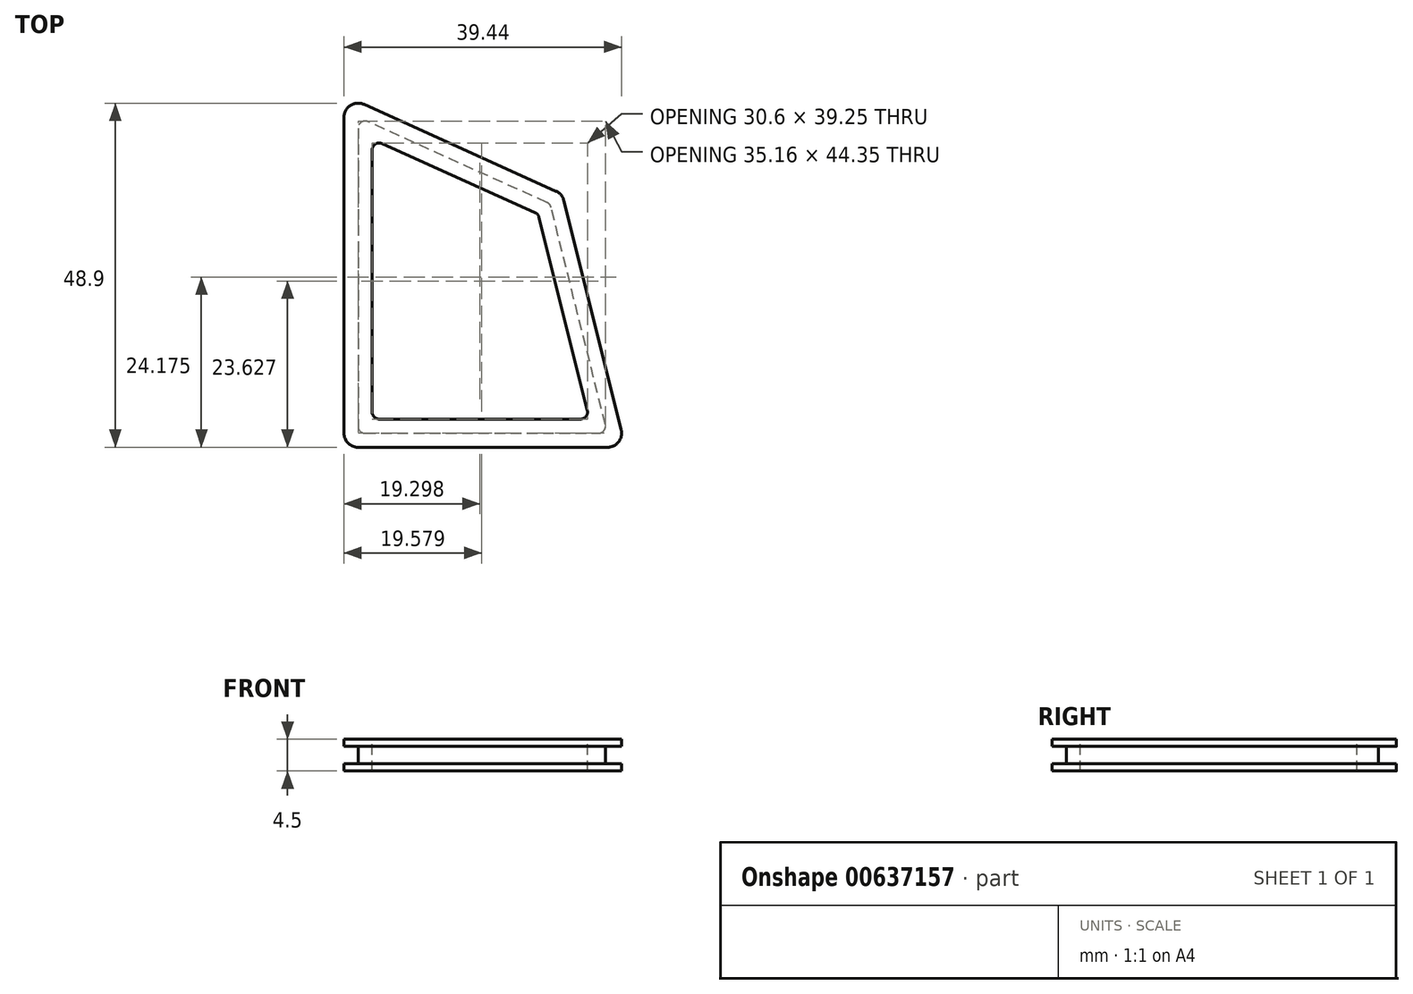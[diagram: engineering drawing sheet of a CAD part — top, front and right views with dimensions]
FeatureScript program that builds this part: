
annotation { "Feature Type Name" : "Feature", "Feature Type Description" : "" }
export const myFeature = defineFeature(function(context is Context, id is Id, definition is map)
    precondition{}
    {
        {
            var Q0;
            Q0=qCreatedBy(makeId("Top.planeOp"),FACE);
            var sketch = newSketch(context, id + "F0", { "sketchPlane" : qUnion([Q0])});
            skLineSegment(sketch, "E0.bottom", {"start": v(17.44, -25) * mm, "end": v(-18, -25) * mm});
            skLineSegment(sketch, "E0.top", {"start": v(10.12, 11.4) * mm, "end": v(-17.18, 23.73) * mm});
            skLineSegment(sketch, "E0.left", {"start": v(19.38, -22.51) * mm, "end": v(11.23, 10.06) * mm});
            skLineSegment(sketch, "E0.right", {"start": v(-20, -23) * mm, "end": v(-20, 21.9) * mm});
            skPoint(sketch, "E0.middle", {"position": v(0, 0) * mm});
            skPoint(sketch, "E1.visualSharp", {"position": v(-20, 25) * mm});
            skArc(sketch, "E1.filletArc", {"start": v(-17.18, 23.73) * mm, "mid": v(-19.08, 23.58) * mm, "end": v(-20, 21.9) * mm});
            skPoint(sketch, "E2.visualSharp", {"position": v(-20, -25) * mm});
            skArc(sketch, "E2.filletArc", {"start": v(-20, -23) * mm, "mid": v(-19.41, -24.41) * mm, "end": v(-18, -25) * mm});
            skPoint(sketch, "E3.visualSharp", {"position": v(20, -25) * mm});
            skArc(sketch, "E3.filletArc", {"start": v(17.44, -25) * mm, "mid": v(19.01, -24.23) * mm, "end": v(19.38, -22.51) * mm});
            skPoint(sketch, "E4.visualSharp", {"position": v(11, 11) * mm});
            skArc(sketch, "E4.filletArc", {"start": v(11.23, 10.06) * mm, "mid": v(10.83, 10.86) * mm, "end": v(10.12, 11.4) * mm});
            skSolve(sketch);
        }
        {
            var Q0;
            Q0=qCreatedBy(makeId("Top.planeOp"),FACE);
            var sketch = newSketch(context, id + "F1", { "sketchPlane" : qUnion([Q0])});
            skLineSegment(sketch, "E5.0.1", {"start": v(8.85, 9.77) * mm, "end": v(-16.59, 21.26) * mm});
            skLineSegment(sketch, "E5.0.3", {"start": v(-18, 20.35) * mm, "end": v(-18, -22) * mm});
            skLineSegment(sketch, "E5.0.5", {"start": v(-17, -23) * mm, "end": v(16.16, -23) * mm});
            skLineSegment(sketch, "E5.0.7", {"start": v(17.13, -21.76) * mm, "end": v(9.41, 9.1) * mm});
            skPoint(sketch, "E6.visualSharp", {"position": v(-18, 21.9) * mm});
            skArc(sketch, "E6.filletArc", {"start": v(-16.59, 21.26) * mm, "mid": v(-17.54, 21.2) * mm, "end": v(-18, 20.35) * mm});
            skPoint(sketch, "E7.visualSharp", {"position": v(9.3, 9.58) * mm});
            skArc(sketch, "E7.filletArc", {"start": v(9.41, 9.1) * mm, "mid": v(9.2, 9.5) * mm, "end": v(8.85, 9.77) * mm});
            skPoint(sketch, "E8.visualSharp", {"position": v(-18, -23) * mm});
            skArc(sketch, "E8.filletArc", {"start": v(-18, -22) * mm, "mid": v(-17.7, -22.7) * mm, "end": v(-17, -23) * mm});
            skPoint(sketch, "E9.visualSharp", {"position": v(17.44, -23) * mm});
            skArc(sketch, "E9.filletArc", {"start": v(16.16, -23) * mm, "mid": v(16.95, -22.62) * mm, "end": v(17.13, -21.76) * mm});
            skSolve(sketch);
        }
        {
            var Q0;
            Q0=makeQuery(id+"F1.imprint","IMPRINT",FACE,{"disambiguationData":[TD([[makeQuery(id+"F1.imprint","IMPRINT",EDGE,{"derivedFrom":sQuery(id+"F1.wireOp",EDGE,"E5.0.1")}),1.0]])]});
            extrude(context, id + "F2", {"entities" : qUnion([Q0]), "depth" : 2.5 * mm, "offsetDistance" : 25 * mm});
        }
        {
            var Q0;
            Q0=makeQuery(id+"F0.imprint","IMPRINT",FACE,{"disambiguationData":[TD([[makeQuery(id+"F0.imprint","IMPRINT",EDGE,{"derivedFrom":sQuery(id+"F0.wireOp",EDGE,"E0.bottom")}),-1.0]])]});
            extrude(context, id + "F3", {"entities" : qUnion([Q0]), "operationType" : NewBodyOperationType.ADD, "oppositeDirection" : true, "depth" : 1 * mm, "offsetDistance" : 25 * mm});
        }
        {
            var Q0;
            Q0=makeQuery(id+"F2.opExtrude","CAP_FACE",FACE,{"disambiguationData":[OSD([sQuery(id+"F1.wireOp",EDGE,"E5.0.1"),sQuery(id+"F1.wireOp",EDGE,"E5.0.3"),sQuery(id+"F1.wireOp",EDGE,"E5.0.5"),sQuery(id+"F1.wireOp",EDGE,"E5.0.7"),sQuery(id+"F1.wireOp",EDGE,"E6.filletArc"),sQuery(id+"F1.wireOp",EDGE,"E7.filletArc"),sQuery(id+"F1.wireOp",EDGE,"E8.filletArc"),sQuery(id+"F1.wireOp",EDGE,"E9.filletArc")])],"isStart":false});
            var sketch = newSketch(context, id + "F4", { "sketchPlane" : qUnion([Q0])});
            skArc(sketch, "E10.0.0", {"start": v(11.23, 10.06) * mm, "mid": v(10.83, 10.86) * mm, "end": v(10.12, 11.4) * mm});
            skLineSegment(sketch, "E10.0.1", {"start": v(10.12, 11.4) * mm, "end": v(-17.18, 23.73) * mm});
            skArc(sketch, "E10.0.2", {"start": v(-17.18, 23.73) * mm, "mid": v(-19.08, 23.58) * mm, "end": v(-20, 21.9) * mm});
            skLineSegment(sketch, "E10.0.3", {"start": v(-20, 21.9) * mm, "end": v(-20, -23) * mm});
            skArc(sketch, "E10.0.4", {"start": v(-20, -23) * mm, "mid": v(-19.41, -24.41) * mm, "end": v(-18, -25) * mm});
            skLineSegment(sketch, "E10.0.5", {"start": v(-18, -25) * mm, "end": v(17.44, -25) * mm});
            skArc(sketch, "E10.0.6", {"start": v(17.44, -25) * mm, "mid": v(19.01, -24.23) * mm, "end": v(19.38, -22.51) * mm});
            skLineSegment(sketch, "E10.0.7", {"start": v(19.38, -22.51) * mm, "end": v(11.23, 10.06) * mm});
            skSolve(sketch);
        }
        {
            var Q0;
            Q0=makeQuery(id+"F4.imprint","IMPRINT",FACE,{"disambiguationData":[TD([[makeQuery(id+"F4.imprint","IMPRINT",EDGE,{"derivedFrom":sQuery(id+"F4.wireOp",EDGE,"E10.0.0")}),1.0]])]});
            var Q1;
            Q1=makeQuery(id+"F4.imprint","IMPRINT",FACE,{"disambiguationData":[TD([[makeQuery(id+"F4.imprint","IMPRINT",EDGE,{"derivedFrom":makeQuery(id+"F2.opExtrude","CAP_EDGE",EDGE,{"disambiguationData":[OSD([sQuery(id+"F1.wireOp",EDGE,"E5.0.1")])],"isStart":false})}),1.0]])]});
            extrude(context, id + "F5", {"entities" : qUnion([Q0, Q1]), "operationType" : NewBodyOperationType.ADD, "depth" : 1 * mm, "offsetDistance" : 25 * mm});
        }
        {
            var Q0;
            Q0=makeQuery(id+"F5.opExtrude","CAP_FACE",FACE,{"disambiguationData":[OSD([sQuery(id+"F4.wireOp",EDGE,"E10.0.0"),sQuery(id+"F4.wireOp",EDGE,"E10.0.1"),sQuery(id+"F4.wireOp",EDGE,"E10.0.2"),sQuery(id+"F4.wireOp",EDGE,"E10.0.3"),sQuery(id+"F4.wireOp",EDGE,"E10.0.4"),sQuery(id+"F4.wireOp",EDGE,"E10.0.5"),sQuery(id+"F4.wireOp",EDGE,"E10.0.6"),sQuery(id+"F4.wireOp",EDGE,"E10.0.7")])],"isStart":false});
            var sketch = newSketch(context, id + "F6", { "sketchPlane" : qUnion([Q0])});
            skLineSegment(sketch, "E11.0", {"start": v(-18, 20.35) * mm, "end": v(-18, -22) * mm});
            skArc(sketch, "E11.1", {"start": v(-16.59, 21.26) * mm, "mid": v(-17.54, 21.2) * mm, "end": v(-18, 20.35) * mm});
            skLineSegment(sketch, "E11.2", {"start": v(8.85, 9.77) * mm, "end": v(-16.59, 21.26) * mm});
            skLineSegment(sketch, "E11.3", {"start": v(-17, -23) * mm, "end": v(16.16, -23) * mm});
            skLineSegment(sketch, "E11.4", {"start": v(17.13, -21.76) * mm, "end": v(9.41, 9.1) * mm});
            skArc(sketch, "E11.5", {"start": v(9.41, 9.1) * mm, "mid": v(9.2, 9.5) * mm, "end": v(8.85, 9.77) * mm});
            skArc(sketch, "E11.6", {"start": v(16.16, -23) * mm, "mid": v(16.95, -22.62) * mm, "end": v(17.13, -21.76) * mm});
            skArc(sketch, "E11.7", {"start": v(-18, -22) * mm, "mid": v(-17.7, -22.7) * mm, "end": v(-17, -23) * mm});
            skLineSegment(sketch, "E12.0", {"start": v(14.57, -19.76) * mm, "end": v(7.7, 7.68) * mm});
            skLineSegment(sketch, "E13.0", {"start": v(7.15, 8.35) * mm, "end": v(-14.59, 18.17) * mm});
            skLineSegment(sketch, "E14.0", {"start": v(-16, 17.26) * mm, "end": v(-16, -20) * mm});
            skLineSegment(sketch, "E15.0", {"start": v(-15, -21) * mm, "end": v(13.6, -21) * mm});
            skPoint(sketch, "E16.visualSharp", {"position": v(14.88, -21) * mm});
            skArc(sketch, "E16.filletArc", {"start": v(13.6, -21) * mm, "mid": v(14.38, -20.62) * mm, "end": v(14.57, -19.76) * mm});
            skPoint(sketch, "E17.visualSharp", {"position": v(-16, -21) * mm});
            skArc(sketch, "E17.filletArc", {"start": v(-16, -20) * mm, "mid": v(-15.7, -20.7) * mm, "end": v(-15, -21) * mm});
            skPoint(sketch, "E18.visualSharp", {"position": v(7.59, 8.15) * mm});
            skArc(sketch, "E18.filletArc", {"start": v(7.7, 7.68) * mm, "mid": v(7.5, 8.08) * mm, "end": v(7.15, 8.35) * mm});
            skPoint(sketch, "E19.visualSharp", {"position": v(-16, 18.8) * mm});
            skArc(sketch, "E19.filletArc", {"start": v(-14.59, 18.17) * mm, "mid": v(-15.54, 18.1) * mm, "end": v(-16, 17.26) * mm});
            skSolve(sketch);
        }
        {
            var Q0;
            Q0=makeQuery(id+"F6.imprint","IMPRINT",FACE,{"disambiguationData":[TD([[makeQuery(id+"F6.imprint","IMPRINT",EDGE,{"derivedFrom":sQuery(id+"F6.wireOp",EDGE,"E12.0")}),1.0]])]});
            extrude(context, id + "F7", {"entities" : qUnion([Q0]), "operationType" : NewBodyOperationType.REMOVE, "oppositeDirection" : true, "depth" : 4.5 * mm, "offsetDistance" : 25 * mm});
        }
    });
